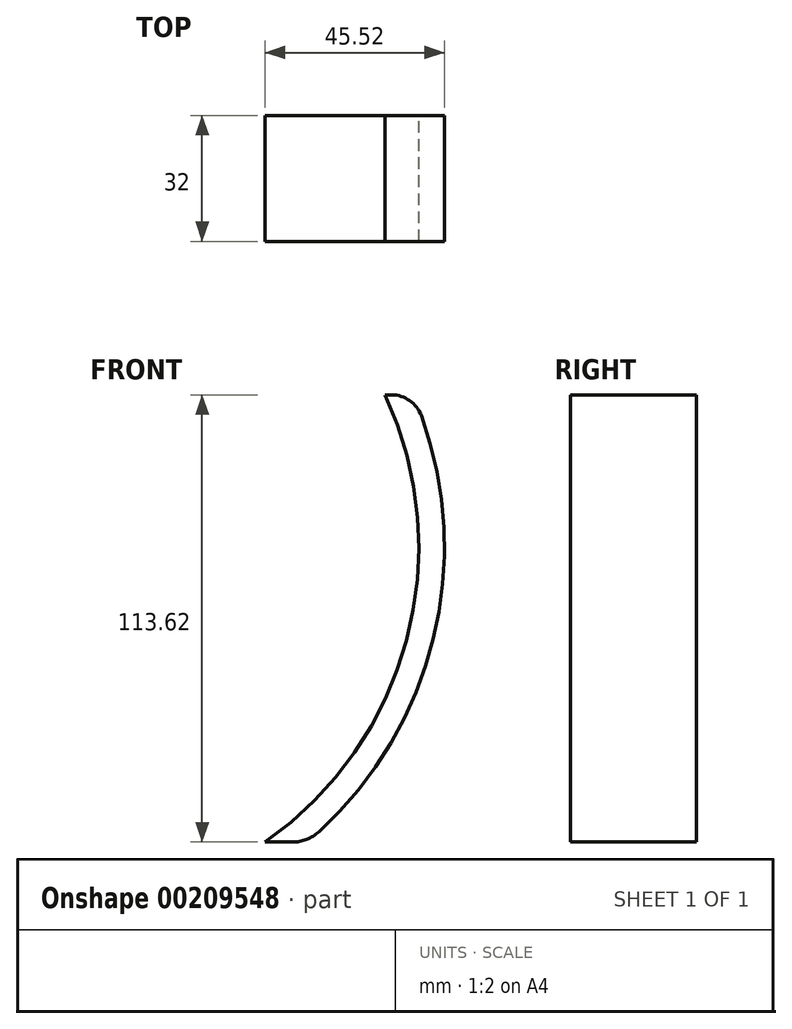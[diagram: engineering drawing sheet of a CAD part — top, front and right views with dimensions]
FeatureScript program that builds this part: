
annotation { "Feature Type Name" : "Feature", "Feature Type Description" : "" }
export const myFeature = defineFeature(function(context is Context, id is Id, definition is map)
    precondition{}
    {
        {
            var Q0;
            Q0=qCreatedBy(makeId("Front.planeOp"),FACE);
            var sketch = newSketch(context, id + "F0", { "sketchPlane" : qUnion([Q0])});
            skArc(sketch, "E0", {"start": v(52.48, -74.95) * mm, "mid": v(88.38, -23.68) * mm, "end": v(82.93, 38.67) * mm});
            skLineSegment(sketch, "E1", {"start": v(0, 0) * mm, "end": v(82.93, 38.67) * mm, "construction": true});
            skLineSegment(sketch, "E2", {"start": v(0, 0) * mm, "end": v(52.48, -74.95) * mm, "construction": true});
            skArc(sketch, "E3", {"start": v(66.12, -72.33) * mm, "mid": v(95.16, -23.41) * mm, "end": v(92.13, 33.4) * mm});
            skLineSegment(sketch, "E4", {"start": v(82.93, 38.67) * mm, "end": v(84.61, 38.67) * mm});
            skLineSegment(sketch, "E5", {"start": v(52.48, -74.95) * mm, "end": v(59.37, -74.95) * mm});
            skPoint(sketch, "E6.visualSharp", {"position": v(90.05, 38.67) * mm});
            skArc(sketch, "E6.filletArc", {"start": v(92.13, 33.4) * mm, "mid": v(89.2, 37.22) * mm, "end": v(84.61, 38.67) * mm});
            skPoint(sketch, "E7.visualSharp", {"position": v(63.14, -74.95) * mm});
            skArc(sketch, "E7.filletArc", {"start": v(59.37, -74.95) * mm, "mid": v(63, -74.27) * mm, "end": v(66.12, -72.33) * mm});
            skSolve(sketch);
        }
        {
            var Q0;
            Q0=makeQuery(id+"F0.imprint","IMPRINT",FACE,{"disambiguationData":[TD([[makeQuery(id+"F0.imprint","IMPRINT",EDGE,{"derivedFrom":sQuery(id+"F0.wireOp",EDGE,"E0")}),-1.0]])]});
            extrude(context, id + "F1", {"entities" : qUnion([Q0]), "depth" : 32 * mm});
        }
    });
